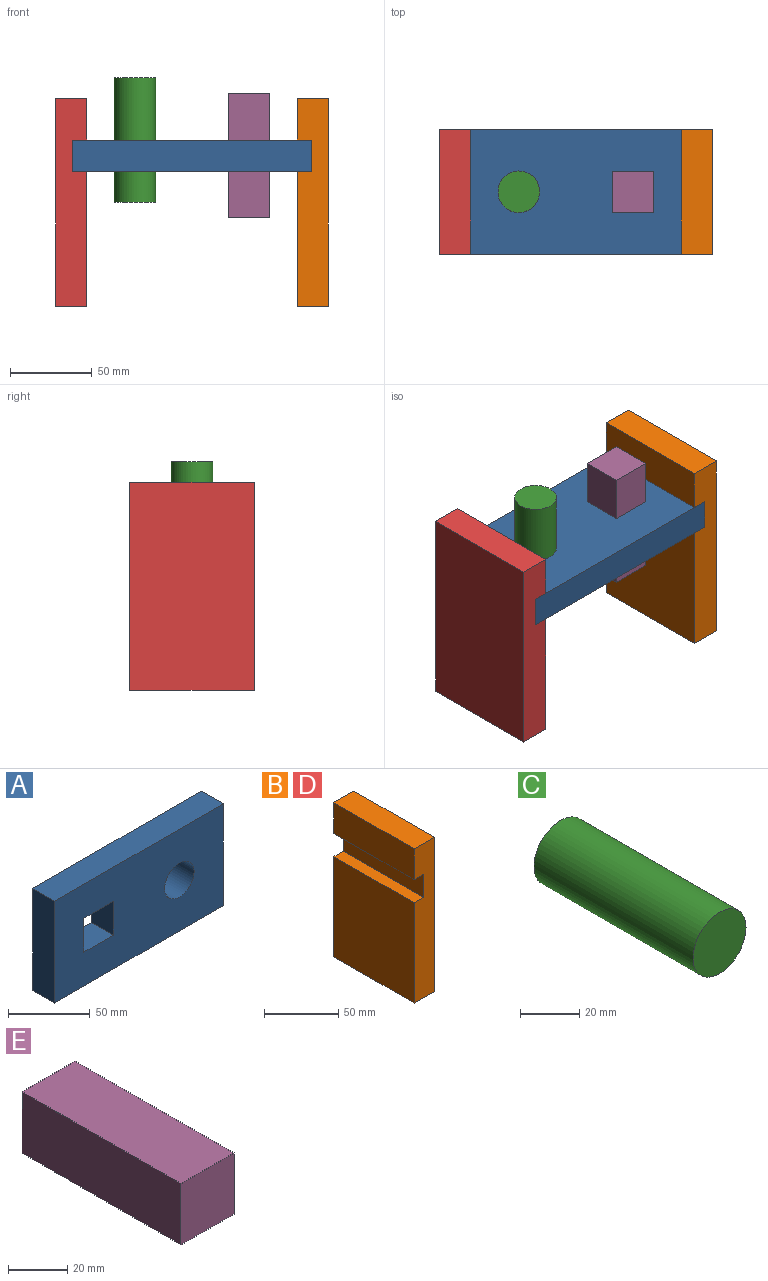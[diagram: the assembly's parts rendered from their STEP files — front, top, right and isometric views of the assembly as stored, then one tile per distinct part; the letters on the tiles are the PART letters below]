
ASSEMBLY  parts=5 mates=4
PART A: 11 faces, bbox 146.1x19.1x76.2 mm
  f0: plane 76.2x19.05mm, normal (-1,0,0), area 1451.6mm2, adj f1,f8,f9,f10
  f1: plane 146.05x19.05mm, normal (0,0,-1), area 2782.3mm2, adj f0,f2,f9,f10
  f2: plane 76.2x19.05mm, normal (1,0,0), area 1451.6mm2, adj f1,f8,f9,f10
  f3: plane 25.4x19.05mm, normal (0,0,1), area 483.9mm2, adj f4,f6,f9,f10
  f4: plane 25.4x19.05mm, normal (1,0,0), area 483.9mm2, adj f3,f5,f9,f10
  f5: plane 25.4x19.05mm, normal (0,0,-1), area 483.9mm2, adj f4,f6,f9,f10
  f6: plane 25.4x19.05mm, normal (-1,0,0), area 483.9mm2, adj f3,f5,f9,f10
  f7: cylinder r=12.7mm len=25.4mm, axis (0,1,0), area 1520.1mm2, adj f9,f10
  f8: plane 146.05x19.05mm, normal (0,0,1), area 2782.3mm2, adj f0,f2,f9,f10
  f9: plane 146.05x76.2mm, normal (0,-1,0), area 9977.1mm2, adj f0,f1,f2,f3,f4,f5,f6,f7
  f10: plane 146.05x76.2mm, normal (0,1,0), area 9977.1mm2, adj f0,f1,f2,f3,f4,f5,f6,f7
PART B: 10 faces, bbox 19.1x76.2x127 mm
  f0: plane 82.54x76.2mm, normal (-1,0,0), area 6289.4mm2, adj f1,f7,f8,f9
  f1: plane 76.2x19.05mm, normal (0,0,-1), area 1451.6mm2, adj f0,f2,f8,f9
  f2: plane 127x76.2mm, normal (1,0,0), area 9677.4mm2, adj f1,f3,f8,f9
  f3: plane 76.2x19.05mm, normal (0,0,1), area 1451.6mm2, adj f2,f4,f8,f9
  f4: plane 76.2x25.4mm, normal (-1,0,0), area 1935.5mm2, adj f3,f5,f8,f9
  f5: plane 76.2x8.89mm, normal (0,0,-1), area 677.4mm2, adj f4,f6,f8,f9
  f6: plane 76.2x19.05mm, normal (-1,0,0), area 1451.6mm2, adj f5,f7,f8,f9
  f7: plane 76.2x8.89mm, normal (0,0,1), area 677.4mm2, adj f0,f6,f8,f9
  f8: plane 127x19.05mm, normal (0,-1,0), area 2249.9mm2, adj f0,f1,f2,f3,f4,f5,f6,f7
  f9: plane 127x19.05mm, normal (0,1,0), area 2249.9mm2, adj f0,f1,f2,f3,f4,f5,f6,f7
PART C: 3 faces, bbox 25.4x76.2x25.4 mm
  f0: cylinder r=12.7mm len=76.2mm, axis (0,1,0), area 6080.5mm2, adj f1,f2
  f1: plane 25.4x25.4mm, normal (0,-1,0), area 506.7mm2, adj f0
  f2: plane 25.4x25.4mm, normal (0,1,0), area 506.7mm2, adj f0
PART D: same geometry as B
PART E: 6 faces, bbox 25.4x76.2x25.4 mm
  f0: plane 76.2x25.4mm, normal (0,0,-1), area 1935.5mm2, adj f1,f3,f4,f5
  f1: plane 76.2x25.4mm, normal (1,0,0), area 1935.5mm2, adj f0,f2,f4,f5
  f2: plane 76.2x25.4mm, normal (0,0,1), area 1935.5mm2, adj f1,f3,f4,f5
  f3: plane 76.2x25.4mm, normal (-1,0,0), area 1935.5mm2, adj f0,f2,f4,f5
  f4: plane 25.4x25.4mm, normal (0,-1,0), area 645.2mm2, adj f0,f1,f2,f3
  f5: plane 25.4x25.4mm, normal (0,1,0), area 645.2mm2, adj f0,f1,f2,f3
PLACE A rot(axis=(0,0.71,0.71),180deg) t=(30.08,25.92,-12.85)mm
PLACE B t=(57.17,64.02,-69.18)mm
PLACE C rot(axis=(-1,0,0),90deg) t=(42.51,15.04,-50.95)mm
PLACE D rot(axis=(0,0,-1),180deg) t=(2.99,-12.18,-69.18)mm
PLACE E rot(axis=(-1,0,0),90deg) t=(27.19,25.92,-60.48)mm
MATE pin_slot E.f2 <-> A.f5  axis (0,1,0) through (65,38.62,-22.38)mm
MATE planar A.f0 <-> B.f6  axis (1,0,0) through (103.1,25.92,-22.38)mm
MATE planar D.f6 <-> A.f2  axis (1,0,0) through (-42.95,25.92,-22.38)mm
MATE pin_slot C.f0 <-> A.f7  axis (0,0,-1) through (-4.85,25.92,-12.85)mm
